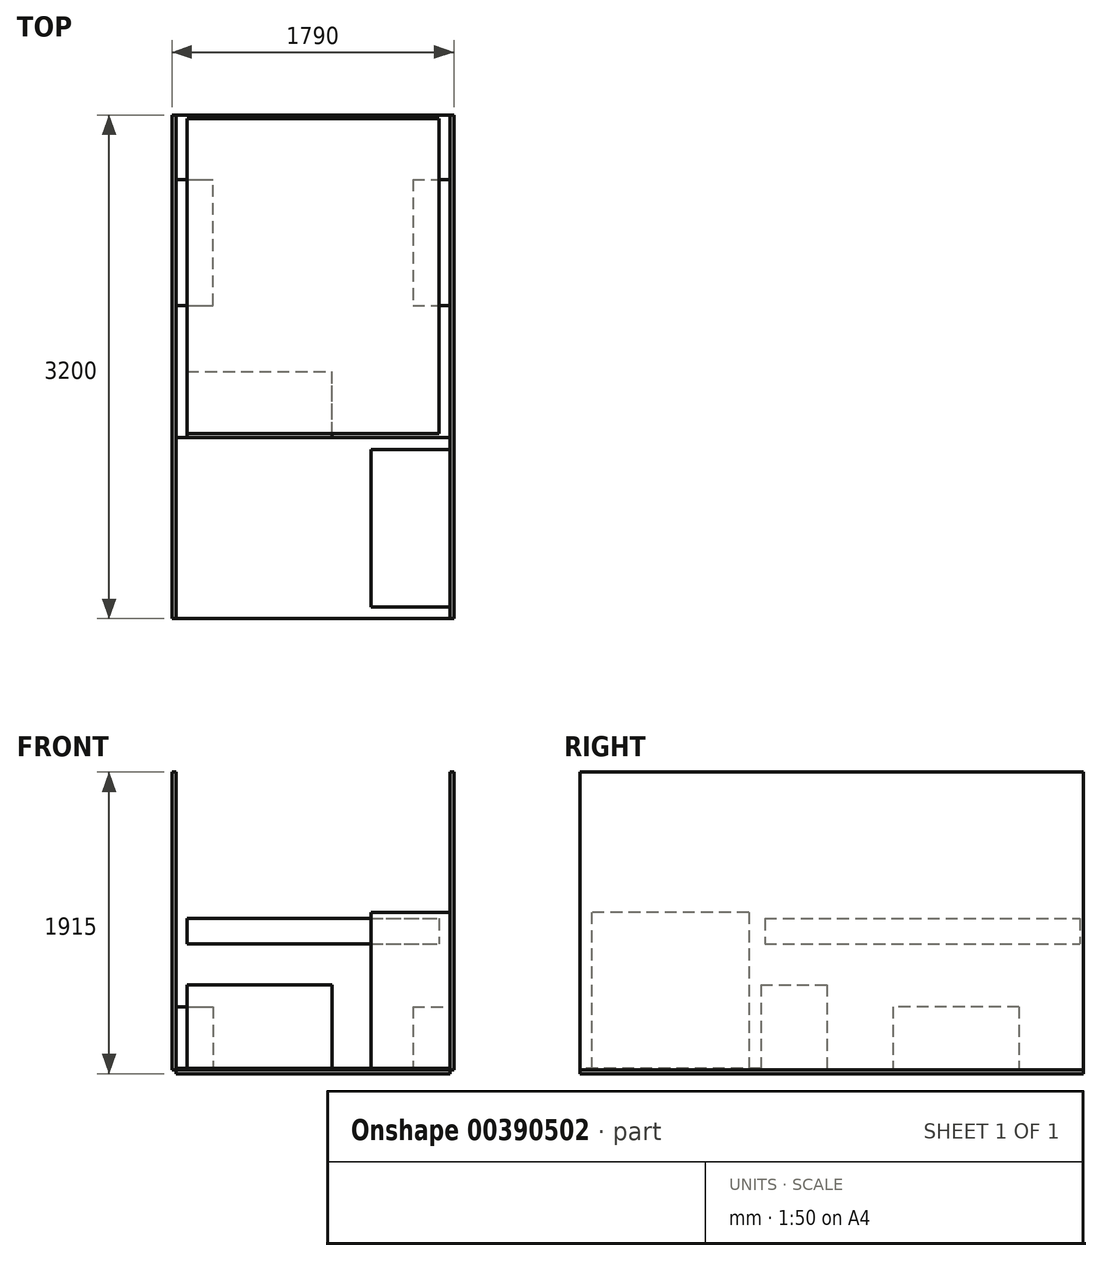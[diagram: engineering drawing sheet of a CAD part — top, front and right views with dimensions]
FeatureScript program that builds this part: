
annotation { "Feature Type Name" : "Feature", "Feature Type Description" : "" }
export const myFeature = defineFeature(function(context is Context, id is Id, definition is map)
    precondition{}
    {
        {
            var Q0;
            Q0=qCreatedBy(makeId("Top.planeOp"),FACE);
            var sketch = newSketch(context, id + "F0", { "sketchPlane" : qUnion([Q0])});
            skLineSegment(sketch, "E0.bottom", {"start": v(0, 3200) * mm, "end": v(1740, 3200) * mm});
            skLineSegment(sketch, "E0.top", {"start": v(0, 0) * mm, "end": v(1740, 0) * mm});
            skLineSegment(sketch, "E0.left", {"start": v(0, 3200) * mm, "end": v(0, 0) * mm});
            skLineSegment(sketch, "E0.right", {"start": v(1740, 3200) * mm, "end": v(1740, 0) * mm});
            skSolve(sketch);
        }
        {
            var Q0;
            Q0=makeQuery(id+"F0.imprint","IMPRINT",FACE,{"disambiguationData":[TD([[makeQuery(id+"F0.imprint","IMPRINT",EDGE,{"derivedFrom":sQuery(id+"F0.wireOp",EDGE,"E0.bottom")}),-1.0]])]});
            extrude(context, id + "F1", {"entities" : qUnion([Q0]), "oppositeDirection" : true, "depth" : 25 * mm});
        }
        {
            var Q0;
            Q0=makeQuery(id+"F1.opExtrude","SWEPT_FACE",FACE,{"disambiguationData":[OSD([sQuery(id+"F0.wireOp",EDGE,"E0.right")])]});
            var sketch = newSketch(context, id + "F2", { "sketchPlane" : qUnion([Q0])});
            skLineSegment(sketch, "E1.bottom", {"start": v(0, 0) * mm, "end": v(3200, 0) * mm});
            skLineSegment(sketch, "E1.top", {"start": v(0, 1890) * mm, "end": v(3200, 1890) * mm});
            skLineSegment(sketch, "E1.left", {"start": v(0, 0) * mm, "end": v(0, 1890) * mm});
            skLineSegment(sketch, "E1.right", {"start": v(3200, 0) * mm, "end": v(3200, 1890) * mm});
            skSolve(sketch);
        }
        {
            var Q0;
            Q0=makeQuery(id+"F1.opExtrude","SWEPT_FACE",FACE,{"disambiguationData":[OSD([sQuery(id+"F0.wireOp",EDGE,"E0.left")])]});
            var sketch = newSketch(context, id + "F3", { "sketchPlane" : qUnion([Q0])});
            skLineSegment(sketch, "E2.bottom", {"start": v(-3200, 1890) * mm, "end": v(0, 1890) * mm});
            skLineSegment(sketch, "E2.top", {"start": v(-3200, 0) * mm, "end": v(0, 0) * mm});
            skLineSegment(sketch, "E2.left", {"start": v(-3200, 1890) * mm, "end": v(-3200, 0) * mm});
            skLineSegment(sketch, "E2.right", {"start": v(0, 1890) * mm, "end": v(0, 0) * mm});
            skSolve(sketch);
        }
        {
            var Q0;
            Q0 = qSketchRegion(id + "F2", true);
            extrude(context, id + "F4", {"entities" : qUnion([Q0]), "depth" : 25 * mm});
        }
        {
            var Q0;
            Q0=makeQuery(id+"F3.imprint","IMPRINT",FACE,{"disambiguationData":[TD([[makeQuery(id+"F3.imprint","IMPRINT",EDGE,{"derivedFrom":sQuery(id+"F3.wireOp",EDGE,"E2.bottom")}),-1.0]])]});
            extrude(context, id + "F5", {"entities" : qUnion([Q0]), "depth" : 25 * mm});
        }
        {
            var Q0;
            Q0=makeQuery(id+"F1.opExtrude","CAP_FACE",FACE,{"disambiguationData":[OSD([sQuery(id+"F0.wireOp",EDGE,"E0.bottom"),sQuery(id+"F0.wireOp",EDGE,"E0.top"),sQuery(id+"F0.wireOp",EDGE,"E0.left"),sQuery(id+"F0.wireOp",EDGE,"E0.right")])],"isStart":true});
            var sketch = newSketch(context, id + "F6", { "sketchPlane" : qUnion([Q0])});
            skLineSegment(sketch, "E3.bottom", {"start": v(0, 1150) * mm, "end": v(1740, 1150) * mm});
            skLineSegment(sketch, "E3.top", {"start": v(0, 0) * mm, "end": v(1740, 0) * mm});
            skLineSegment(sketch, "E3.left", {"start": v(0, 1150) * mm, "end": v(0, 0) * mm});
            skLineSegment(sketch, "E3.right", {"start": v(1740, 1150) * mm, "end": v(1740, 0) * mm});
            skSolve(sketch);
        }
        {
            var Q0;
            Q0=makeQuery(id+"F6.imprint","IMPRINT",FACE,{"disambiguationData":[TD([[makeQuery(id+"F6.imprint","IMPRINT",EDGE,{"derivedFrom":sQuery(id+"F6.wireOp",EDGE,"E3.bottom")}),-1.0]])]});
            extrude(context, id + "F7", {"entities" : qUnion([Q0]), "depth" : 10 * mm});
        }
        {
            var Q0;
            Q0=makeQuery(id+"F1.opExtrude","CAP_FACE",FACE,{"disambiguationData":[OSD([sQuery(id+"F0.wireOp",EDGE,"E0.bottom"),sQuery(id+"F0.wireOp",EDGE,"E0.top"),sQuery(id+"F0.wireOp",EDGE,"E0.left"),sQuery(id+"F0.wireOp",EDGE,"E0.right")])],"isStart":true});
            var sketch = newSketch(context, id + "F8", { "sketchPlane" : qUnion([Q0])});
            skLineSegment(sketch, "E4.bottom", {"start": v(0, 1990) * mm, "end": v(235, 1990) * mm});
            skLineSegment(sketch, "E4.top", {"start": v(0, 2790) * mm, "end": v(235, 2790) * mm});
            skLineSegment(sketch, "E4.left", {"start": v(0, 1990) * mm, "end": v(0, 2790) * mm});
            skLineSegment(sketch, "E4.right", {"start": v(235, 1990) * mm, "end": v(235, 2790) * mm});
            skSolve(sketch);
        }
        {
            var Q0;
            Q0=makeQuery(id+"F8.imprint","IMPRINT",FACE,{"disambiguationData":[TD([[makeQuery(id+"F8.imprint","IMPRINT",EDGE,{"derivedFrom":sQuery(id+"F8.wireOp",EDGE,"E4.bottom")}),1.0]])]});
            extrude(context, id + "F9", {"entities" : qUnion([Q0]), "depth" : 400 * mm});
        }
        {
            var Q0;
            Q0=makeQuery(id+"F1.opExtrude","CAP_FACE",FACE,{"disambiguationData":[OSD([sQuery(id+"F0.wireOp",EDGE,"E0.bottom"),sQuery(id+"F0.wireOp",EDGE,"E0.top"),sQuery(id+"F0.wireOp",EDGE,"E0.left"),sQuery(id+"F0.wireOp",EDGE,"E0.right")])],"isStart":true});
            var sketch = newSketch(context, id + "F10", { "sketchPlane" : qUnion([Q0])});
            skLineSegment(sketch, "E5.bottom", {"start": v(1505, 2790) * mm, "end": v(1740, 2790) * mm});
            skLineSegment(sketch, "E5.top", {"start": v(1505, 1990) * mm, "end": v(1740, 1990) * mm});
            skLineSegment(sketch, "E5.left", {"start": v(1505, 2790) * mm, "end": v(1505, 1990) * mm});
            skLineSegment(sketch, "E5.right", {"start": v(1740, 2790) * mm, "end": v(1740, 1990) * mm});
            skSolve(sketch);
        }
        {
            var Q0;
            Q0=makeQuery(id+"F10.imprint","IMPRINT",FACE,{"disambiguationData":[TD([[makeQuery(id+"F10.imprint","IMPRINT",EDGE,{"derivedFrom":sQuery(id+"F10.wireOp",EDGE,"E5.bottom")}),-1.0]])]});
            extrude(context, id + "F11", {"entities" : qUnion([Q0]), "depth" : 400 * mm});
        }
        {
            var Q0;
            Q0=qCreatedBy(makeId("Top.planeOp"),FACE);
            cPlane(context, id + "F12", {"entities" : qUnion([Q0]), "cplaneType" : CPlaneType.OFFSET, "offset" : 800 * mm, "width" : 150 * mm, "height" : 150 * mm});
        }
        {
            var Q0;
            Q0=qCreatedBy(id+"F12.planeOp",FACE);
            var sketch = newSketch(context, id + "F13", { "sketchPlane" : qUnion([Q0])});
            skLineSegment(sketch, "E6.bottom", {"start": v(70, 1175) * mm, "end": v(1670, 1175) * mm});
            skLineSegment(sketch, "E6.top", {"start": v(70, 3175) * mm, "end": v(1670, 3175) * mm});
            skLineSegment(sketch, "E6.left", {"start": v(70, 1175) * mm, "end": v(70, 3175) * mm});
            skLineSegment(sketch, "E6.right", {"start": v(1670, 1175) * mm, "end": v(1670, 3175) * mm});
            skSolve(sketch);
        }
        {
            var Q0;
            Q0=makeQuery(id+"F13.imprint","IMPRINT",FACE,{"disambiguationData":[TD([[makeQuery(id+"F13.imprint","IMPRINT",EDGE,{"derivedFrom":sQuery(id+"F13.wireOp",EDGE,"E6.bottom")}),1.0]])]});
            extrude(context, id + "F14", {"entities" : qUnion([Q0]), "depth" : 160 * mm});
        }
        {
            var Q0;
            Q0=qCreatedBy(makeId("Top.planeOp"),FACE);
            var sketch = newSketch(context, id + "F15", { "sketchPlane" : qUnion([Q0])});
            skLineSegment(sketch, "E7.bottom", {"start": v(1240, 1075) * mm, "end": v(1740, 1075) * mm});
            skLineSegment(sketch, "E7.top", {"start": v(1240, 75) * mm, "end": v(1740, 75) * mm});
            skLineSegment(sketch, "E7.left", {"start": v(1240, 1075) * mm, "end": v(1240, 75) * mm});
            skLineSegment(sketch, "E7.right", {"start": v(1740, 1075) * mm, "end": v(1740, 75) * mm});
            skSolve(sketch);
        }
        {
            var Q0;
            Q0 = qSketchRegion(id + "F15", true);
            extrude(context, id + "F16", {"entities" : qUnion([Q0]), "depth" : 1000 * mm});
        }
        {
            var Q0;
            Q0=makeQuery(id+"F1.opExtrude","CAP_FACE",FACE,{"disambiguationData":[OSD([sQuery(id+"F0.wireOp",EDGE,"E0.bottom"),sQuery(id+"F0.wireOp",EDGE,"E0.top"),sQuery(id+"F0.wireOp",EDGE,"E0.left"),sQuery(id+"F0.wireOp",EDGE,"E0.right")])],"isStart":true});
            var sketch = newSketch(context, id + "F17", { "sketchPlane" : qUnion([Q0])});
            skLineSegment(sketch, "E8.bottom", {"start": v(70, 1150) * mm, "end": v(990, 1150) * mm});
            skLineSegment(sketch, "E8.top", {"start": v(70, 1570) * mm, "end": v(990, 1570) * mm});
            skLineSegment(sketch, "E8.left", {"start": v(70, 1150) * mm, "end": v(70, 1570) * mm});
            skLineSegment(sketch, "E8.right", {"start": v(990, 1150) * mm, "end": v(990, 1570) * mm});
            skSolve(sketch);
        }
        {
            var Q0;
            Q0=makeQuery(id+"F17.imprint","IMPRINT",FACE,{"disambiguationData":[TD([[makeQuery(id+"F17.imprint","IMPRINT",EDGE,{"derivedFrom":sQuery(id+"F17.wireOp",EDGE,"E8.bottom")}),1.0]])]});
            extrude(context, id + "F18", {"entities" : qUnion([Q0]), "depth" : 540 * mm});
        }
    });
